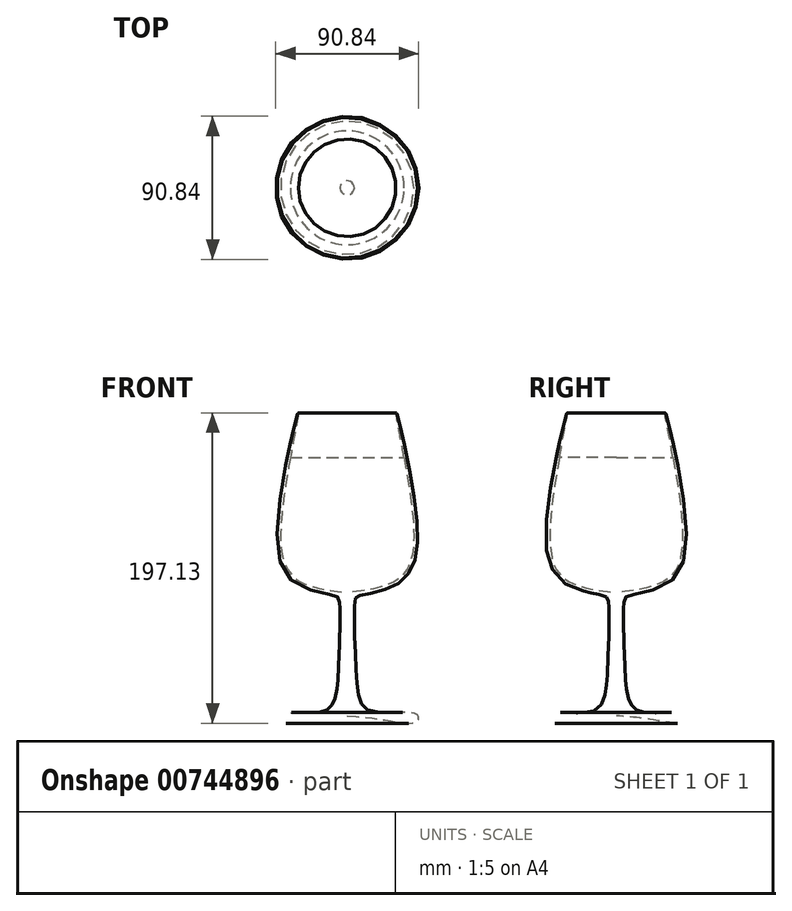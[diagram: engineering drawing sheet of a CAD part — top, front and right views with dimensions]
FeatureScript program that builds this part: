
annotation { "Feature Type Name" : "Feature", "Feature Type Description" : "" }
export const myFeature = defineFeature(function(context is Context, id is Id, definition is map)
    precondition{}
    {
        {
            var Q0;
            Q0=qCreatedBy(makeId("Front.planeOp"),FACE);
            var sketch = newSketch(context, id + "F0", { "sketchPlane" : qUnion([Q0])});
            skFitSpline(sketch, "E0", {"points": [v(0, 4.5) * mm, v(37.06, 0) * mm, v(44.83, 1.71) * mm, v(44.2, 5.46) * mm, v(15.98, 7.3) * mm, v(7.6, 16.3) * mm, v(5.13, 44.82) * mm, v(5.03, 78.3) * mm, v(7.53, 80.8) * mm, v(33.65, 89.49) * mm, v(43.87, 133.02) * mm, v(31.2, 197.02) * mm, v(31.14, 196.02) * mm, v(41.51, 132.6) * mm, v(33.22, 91.99) * mm, v(6.68, 83.69) * mm, v(0, 82.95) * mm], "startDerivative": vector(681.5, -24.85) * mm, "endDerivative": vector(-153.6, -5.3) * mm});
            skLineSegment(sketch, "E1", {"start": v(0, -34.47) * mm, "end": v(0, 242.48) * mm, "construction": true});
            skLineSegment(sketch, "E2", {"start": v(0, 82.95) * mm, "end": v(0, 4.5) * mm});
            skLineSegment(sketch, "E3", {"start": v(0, 168.77) * mm, "end": v(36.1, 168.77) * mm});
            skLineSegment(sketch, "E4", {"start": v(0, 168.77) * mm, "end": v(0, 82.95) * mm});
            skLineSegment(sketch, "E5", {"start": v(46.68, 183.4) * mm, "end": v(46.68, -12.23) * mm, "construction": true});
            skArc(sketch, "E6", {"start": v(31.57, 196.19) * mm, "mid": v(31.07, 197.56) * mm, "end": v(31.13, 196.1) * mm});
            skSolve(sketch);
        }
        {
            var Q0;
            Q0=makeQuery(id+"F0.imprint","IMPRINT",FACE,{"disambiguationData":[TD([[makeQuery(id+"F0.imprint","IMPRINT",EDGE,{"derivedFrom":sQuery(id+"F0.wireOp",EDGE,"E0")}),1.0]])]});
            var Q1;
            Q1=sQuery(id+"F0.wireOp",EDGE,"E1");
            revolve(context, id + "F1", {"surfaceOperationType" : NewSurfaceOperationType.NEW, "entities" : qUnion([Q0]), "axis" : qUnion([Q1]), "revolveType" : RevolveType.FULL});
        }
        {
            var Q0;
            {var subQ2=sQuery(id+"F0.wireOp",EDGE,"E3");Q0=makeQuery(id+"F0.imprint","IMPRINT",FACE,{"disambiguationData":[TD([[makeQuery(id+"F0.imprint","IMPRINT",EDGE,{"derivedFrom":subQ2}),-1.0]])]});}
            var Q1;
            Q1=sQuery(id+"F0.wireOp",EDGE,"E1");
            revolve(context, id + "F2", {"surfaceOperationType" : NewSurfaceOperationType.NEW, "entities" : qUnion([Q0]), "axis" : qUnion([Q1]), "revolveType" : RevolveType.FULL});
        }
    });
